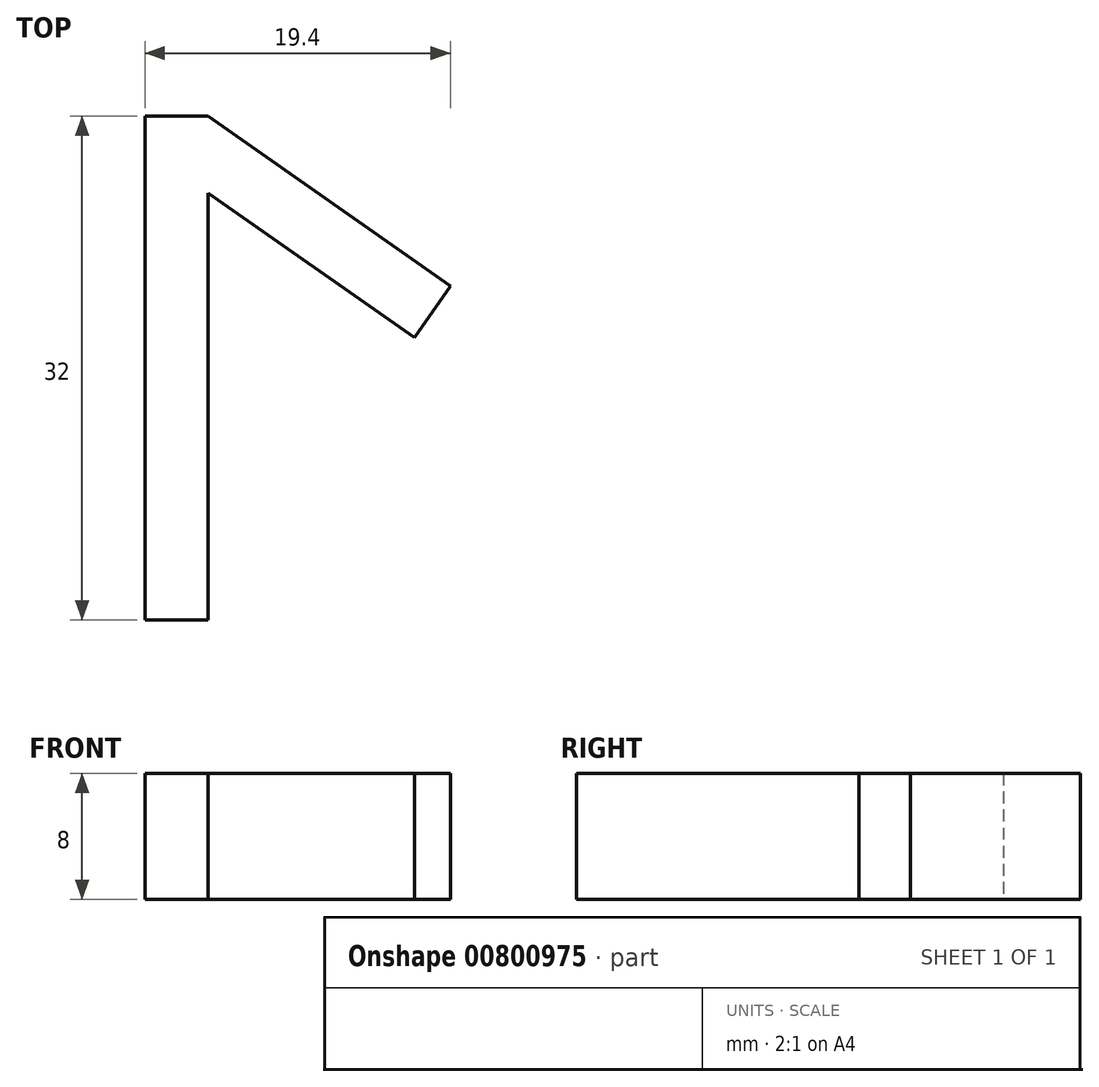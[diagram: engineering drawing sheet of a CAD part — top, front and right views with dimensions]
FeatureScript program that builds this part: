
annotation { "Feature Type Name" : "Feature", "Feature Type Description" : "" }
export const myFeature = defineFeature(function(context is Context, id is Id, definition is map)
    precondition{}
    {
        {
            var Q0;
            Q0=qCreatedBy(makeId("Top.planeOp"),FACE);
            var sketch = newSketch(context, id + "F0", { "sketchPlane" : qUnion([Q0])});
            skLineSegment(sketch, "E0", {"start": v(0, 0) * mm, "end": v(0, -32) * mm});
            skLineSegment(sketch, "E1", {"start": v(0, -32) * mm, "end": v(4, -32) * mm});
            skLineSegment(sketch, "E2", {"start": v(4, -32) * mm, "end": v(4, -4.88) * mm});
            skLineSegment(sketch, "E3", {"start": v(4, -4.88) * mm, "end": v(17.1, -14.06) * mm});
            skLineSegment(sketch, "E4", {"start": v(17.1, -14.06) * mm, "end": v(19.4, -10.78) * mm});
            skLineSegment(sketch, "E5", {"start": v(19.4, -10.78) * mm, "end": v(4, 0) * mm});
            skLineSegment(sketch, "E6", {"start": v(4, 0) * mm, "end": v(0, 0) * mm});
            skSolve(sketch);
        }
        {
            var Q0;
            Q0=makeQuery(id+"F0.imprint","IMPRINT",FACE,{"disambiguationData":[TD([[makeQuery(id+"F0.imprint","IMPRINT",EDGE,{"derivedFrom":sQuery(id+"F0.wireOp",EDGE,"E0")}),1.0]])]});
            extrude(context, id + "F1", {"entities" : qUnion([Q0]), "depth" : 8 * mm, "offsetDistance" : 25 * mm});
        }
    });
